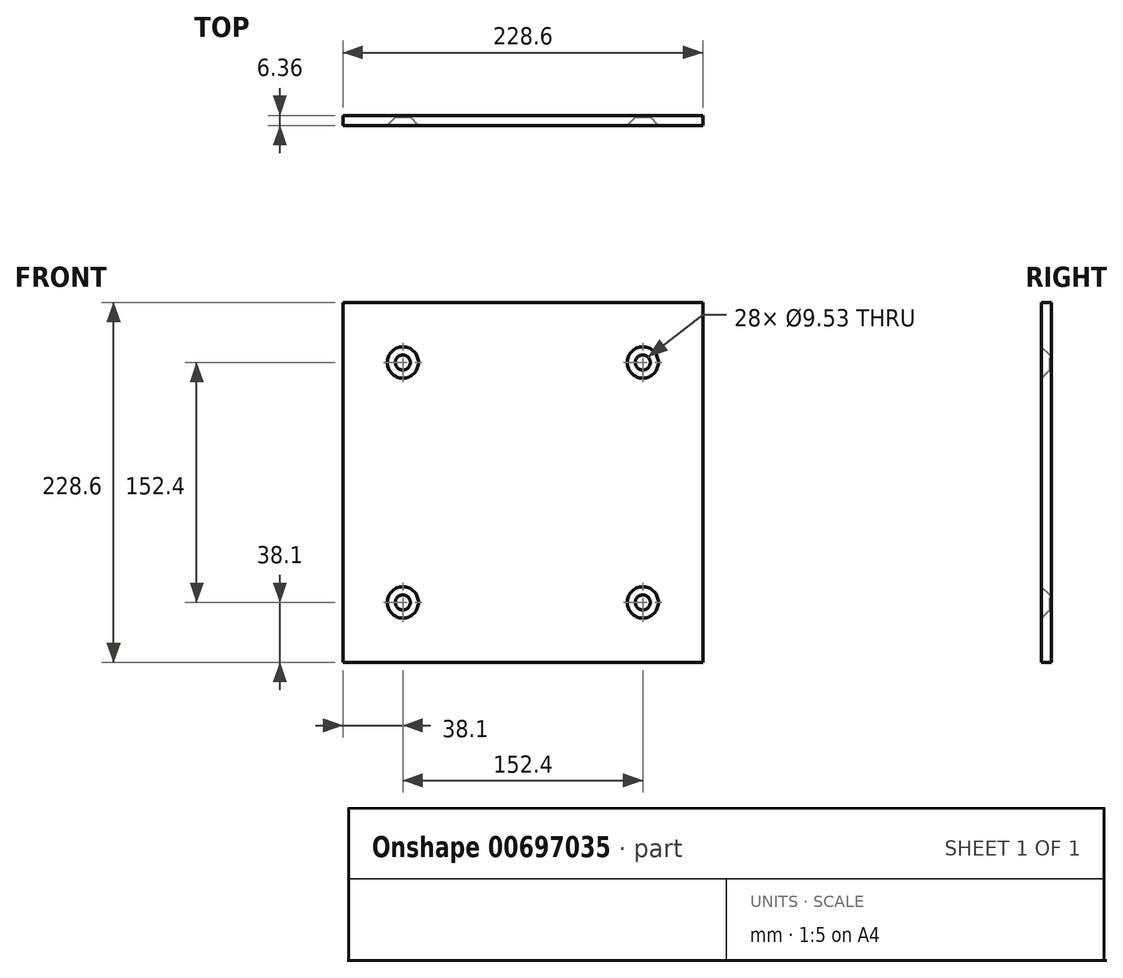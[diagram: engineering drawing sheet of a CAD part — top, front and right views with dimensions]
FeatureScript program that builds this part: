
annotation { "Feature Type Name" : "Feature", "Feature Type Description" : "" }
export const myFeature = defineFeature(function(context is Context, id is Id, definition is map)
    precondition{}
    {
        {
            var Q0;
            Q0=qCreatedBy(makeId("Front.planeOp"),FACE);
            var sketch = newSketch(context, id + "F0", { "sketchPlane" : qUnion([Q0])});
            skLineSegment(sketch, "E0.bottom", {"start": v(114.3, 114.3) * mm, "end": v(-114.3, 114.3) * mm});
            skLineSegment(sketch, "E0.top", {"start": v(114.3, -114.3) * mm, "end": v(-114.3, -114.3) * mm});
            skLineSegment(sketch, "E0.left", {"start": v(114.3, 114.3) * mm, "end": v(114.3, -114.3) * mm});
            skLineSegment(sketch, "E0.right", {"start": v(-114.3, 114.3) * mm, "end": v(-114.3, -114.3) * mm});
            skPoint(sketch, "E0.middle", {"position": v(0, 0) * mm});
            skSolve(sketch);
        }
        {
            var Q0;
            Q0 = qSketchRegion(id + "F0", true);
            extrude(context, id + "F1", {"entities" : qUnion([Q0]), "depth" : 6.35 * mm, "offsetDistance" : 25.4 * mm, "symmetric" : true});
        }
        {
            var Q0;
            Q0=makeQuery(id+"F1.opExtrude","CAP_FACE",FACE,{"disambiguationData":[OSD([sQuery(id+"F0.wireOp",EDGE,"E0.bottom"),sQuery(id+"F0.wireOp",EDGE,"E0.top"),sQuery(id+"F0.wireOp",EDGE,"E0.left"),sQuery(id+"F0.wireOp",EDGE,"E0.right")])],"isStart":false});
            var sketch = newSketch(context, id + "F2", { "sketchPlane" : qUnion([Q0])});
            skLineSegment(sketch, "E1.bottom", {"start": v(76.2, 76.2) * mm, "end": v(-76.2, 76.2) * mm});
            skLineSegment(sketch, "E1.top", {"start": v(76.2, -76.2) * mm, "end": v(-76.2, -76.2) * mm});
            skLineSegment(sketch, "E1.left", {"start": v(76.2, 76.2) * mm, "end": v(76.2, -76.2) * mm});
            skLineSegment(sketch, "E1.right", {"start": v(-76.2, 76.2) * mm, "end": v(-76.2, -76.2) * mm});
            skPoint(sketch, "E1.middle", {"position": v(0, 0) * mm});
            skSolve(sketch);
        }
        {
            var Q0;
            Q0=sQuery(id+"F2.wireOp",VERTEX,"E1.right.start");
            var Q1;
            Q1=sQuery(id+"F2.wireOp",VERTEX,"E1.left.start");
            var Q2;
            Q2=sQuery(id+"F2.wireOp",VERTEX,"E1.left.end");
            var Q3;
            Q3=sQuery(id+"F2.wireOp",VERTEX,"E1.top.end");
            var Q4;
            Q4=makeQuery(id+"F1.opExtrude","SWEPT_BODY",BODY,{"disambiguationData":[OSD([sQuery(id+"F0.wireOp",EDGE,"E0.bottom"),sQuery(id+"F0.wireOp",EDGE,"E0.top"),sQuery(id+"F0.wireOp",EDGE,"E0.left"),sQuery(id+"F0.wireOp",EDGE,"E0.right")])]});
            hole(context, id + "F3", {"style" : HoleStyle.C_SINK, "endStyle" : HoleEndStyle.THROUGH, "holeDiameter" : 9.52 * mm, "cSinkDiameter" : 19.84 * mm, "cSinkAngle" : 90 * degree, "majorDiameter" : 6.35 * mm, "isTappedThrough" : true, "tappedDepth" : 12.7 * mm, "tapClearance" : 3, "startFromSketch" : true, "locations" : qUnion([Q0, Q1, Q2, Q3]), "scope" : qUnion([Q4])});
        }
    });
